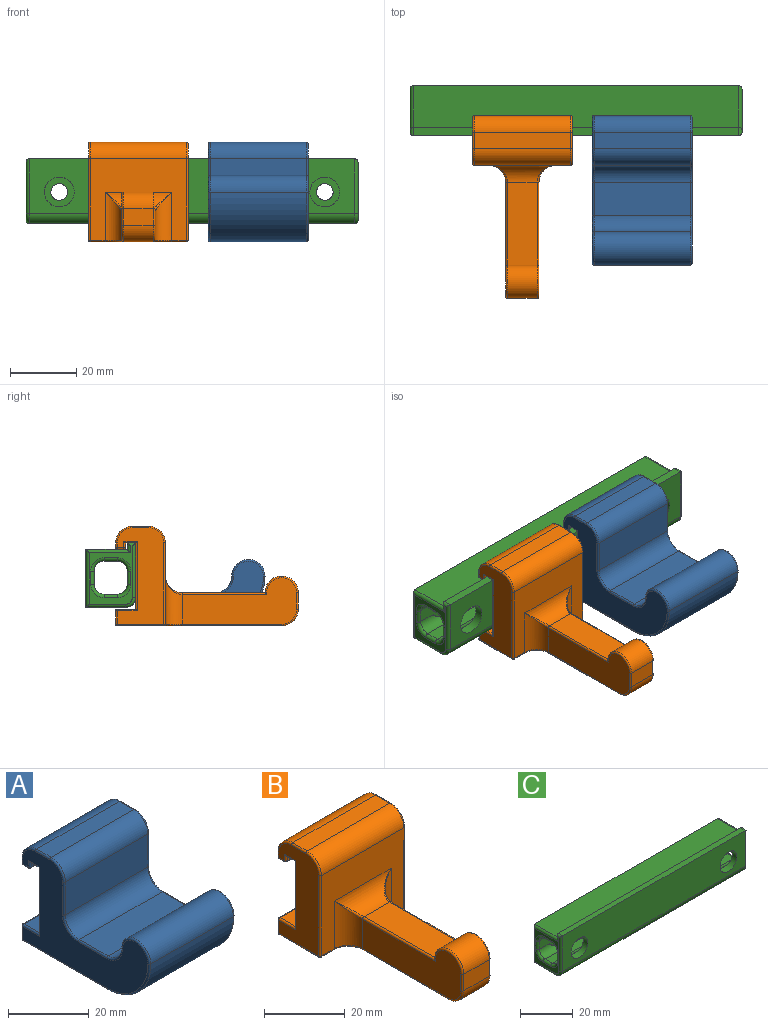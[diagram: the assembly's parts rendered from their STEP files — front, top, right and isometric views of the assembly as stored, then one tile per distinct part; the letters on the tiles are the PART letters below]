
ASSEMBLY  parts=3 mates=4
PART A: 65 faces, bbox 30x46.6x31.6 mm
  f0: plane 29x10mm, normal (0,-1,0), area 290mm2, adj f16,f18,f34,f50
  f1: plane 29x1.5mm, normal (0,1,0), area 43.5mm2, adj f17,f26,f42,f63
  f2: plane 44x29mm, normal (-1,0,0), area 594.5mm2, adj f19,f20,f21,f22,f23,f24,f25,f26
  f3: plane 29x5mm, normal (0,0,1), area 145mm2, adj f17,f18,f30,f46
  f4: plane 29.5x29mm, normal (0,0,-1), area 855.5mm2, adj f15,f25,f43,f54
  f5: plane 44x29mm, normal (1,0,0), area 594.5mm2, adj f36,f37,f38,f39,f40,f41,f42,f43
  f6: plane 29x4mm, normal (0,1,0), area 116mm2, adj f23,f41,f54,f57
  f7: plane 29x2mm, normal (0,0,-1), area 58mm2, adj f24,f40,f60,f63
  f8: plane 29x1.5mm, normal (0,-1,0), area 43.5mm2, adj f9,f22,f38,f60
  f9: plane 29x3mm, normal (0,0,-1), area 87mm2, adj f8,f10,f20,f36
  f10: plane 29x20mm, normal (0,1,0), area 580mm2, adj f9,f11,f19,f37
  f11: plane 29x5.5mm, normal (0,0,1), area 159.5mm2, adj f10,f21,f39,f57
  f12: plane 29x10mm, normal (0,0,1), area 290mm2, adj f13,f16,f33,f51
  f13: cylinder r=5mm len=29mm, axis (1,0,0), area 227.8mm2, adj f12,f14,f31,f49
  f14: cylinder r=5mm len=29mm, axis (1,0,0), area 455.5mm2, adj f13,f15,f29,f47
  f15: cylinder r=15mm len=29mm, axis (1,0,0), area 683.3mm2, adj f4,f14,f27,f45
  f16: cylinder r=5mm len=29mm, axis (-1,0,0), area 227.8mm2, adj f0,f12,f35,f52
  f17: cylinder r=5mm len=29mm, axis (-1,0,0), area 227.8mm2, adj f1,f3,f28,f44
  f18: cylinder r=5mm len=29mm, axis (1,0,0), area 227.8mm2, adj f0,f3,f32,f48
  f19: cylinder r=0.5mm len=21mm, axis (0,0,-1), area 16mm2, adj f2,f10,f20,f21
  f20: cylinder r=0.5mm len=4mm, axis (0,-1,0), area 2.6mm2, adj f2,f9,f19,f22
  f21: cylinder r=0.5mm len=6mm, axis (0,1,0), area 4.5mm2, adj f2,f11,f19,f58
  f22: cylinder r=0.5mm len=2mm, axis (0,0,1), area 1.3mm2, adj f2,f8,f20,f61
  f23: cylinder r=0.5mm len=4mm, axis (0,0,-1), area 3.1mm2, adj f2,f6,f55,f58
  f24: cylinder r=0.5mm len=2mm, axis (0,-1,0), area 1.6mm2, adj f2,f7,f61,f64
  f25: cylinder r=0.5mm len=29.5mm, axis (0,-1,0), area 23.2mm2, adj f2,f4,f27,f55
  f26: cylinder r=0.5mm len=1.5mm, axis (0,0,-1), area 1.2mm2, adj f1,f2,f28,f64
  f27: torus R=14.5mm, axis (-1,0,0), area 18.3mm2, adj f2,f15,f25,f29
  f28: torus R=4.5mm, axis (-1,0,0), area 5.9mm2, adj f2,f17,f26,f30
  f29: torus R=4.5mm, axis (-1,0,0), area 11.9mm2, adj f2,f14,f27,f31
  f30: cylinder r=0.5mm len=5mm, axis (0,1,0), area 3.9mm2, adj f2,f3,f28,f32
  f31: torus R=5.5mm, axis (-1,0,0), area 6.4mm2, adj f2,f13,f29,f33
  f32: torus R=4.5mm, axis (-1,0,0), area 5.9mm2, adj f2,f18,f30,f34
  f33: cylinder r=0.5mm len=10mm, axis (0,-1,0), area 7.9mm2, adj f2,f12,f31,f35
  f34: cylinder r=0.5mm len=10mm, axis (0,0,1), area 7.9mm2, adj f0,f2,f32,f35
  f35: torus R=5.5mm, axis (-1,0,0), area 6.4mm2, adj f2,f16,f33,f34
  f36: cylinder r=0.5mm len=4mm, axis (0,-1,0), area 2.6mm2, adj f5,f9,f37,f38
  f37: cylinder r=0.5mm len=21mm, axis (0,0,-1), area 16mm2, adj f5,f10,f36,f39
  f38: cylinder r=0.5mm len=2mm, axis (0,0,1), area 1.3mm2, adj f5,f8,f36,f59
  f39: cylinder r=0.5mm len=6mm, axis (0,1,0), area 4.5mm2, adj f5,f11,f37,f56
  f40: cylinder r=0.5mm len=2mm, axis (0,-1,0), area 1.6mm2, adj f5,f7,f59,f62
  f41: cylinder r=0.5mm len=4mm, axis (0,0,1), area 3.1mm2, adj f5,f6,f53,f56
  f42: cylinder r=0.5mm len=1.5mm, axis (0,0,1), area 1.2mm2, adj f1,f5,f44,f62
  f43: cylinder r=0.5mm len=29.5mm, axis (0,1,0), area 23.2mm2, adj f4,f5,f45,f53
  f44: torus R=4.5mm, axis (-1,0,0), area 5.9mm2, adj f5,f17,f42,f46
  f45: torus R=14.5mm, axis (-1,0,0), area 18.3mm2, adj f5,f15,f43,f47
  f46: cylinder r=0.5mm len=5mm, axis (0,-1,0), area 3.9mm2, adj f3,f5,f44,f48
  f47: torus R=4.5mm, axis (-1,0,0), area 11.9mm2, adj f5,f14,f45,f49
  f48: torus R=4.5mm, axis (-1,0,0), area 5.9mm2, adj f5,f18,f46,f50
  f49: torus R=5.5mm, axis (-1,0,0), area 6.4mm2, adj f5,f13,f47,f51
  f50: cylinder r=0.5mm len=10mm, axis (0,0,-1), area 7.9mm2, adj f0,f5,f48,f52
  f51: cylinder r=0.5mm len=10mm, axis (0,1,0), area 7.9mm2, adj f5,f12,f49,f52
  f52: torus R=5.5mm, axis (-1,0,0), area 6.4mm2, adj f5,f16,f50,f51
  f53: sphere r=0.5mm, area 0.4mm2, adj f41,f43,f54
  f54: cylinder r=0.5mm len=29mm, axis (1,0,0), area 22.8mm2, adj f4,f6,f53,f55
  f55: sphere r=0.5mm, area 0.4mm2, adj f23,f25,f54
  f56: sphere r=0.5mm, area 0.4mm2, adj f39,f41,f57
  f57: cylinder r=0.5mm len=29mm, axis (-1,0,0), area 22.8mm2, adj f6,f11,f56,f58
  f58: sphere r=0.5mm, area 0.4mm2, adj f21,f23,f57
  f59: sphere r=0.5mm, area 0.4mm2, adj f38,f40,f60
  f60: cylinder r=0.5mm len=29mm, axis (1,0,0), area 22.8mm2, adj f7,f8,f59,f61
  f61: sphere r=0.5mm, area 0.4mm2, adj f22,f24,f60
  f62: sphere r=0.5mm, area 0.4mm2, adj f40,f42,f63
  f63: cylinder r=0.5mm len=29mm, axis (-1,0,0), area 22.8mm2, adj f1,f7,f62,f64
  f64: sphere r=0.5mm, area 0.4mm2, adj f24,f26,f63
PART B: 77 faces, bbox 30x55.8x30.8 mm
  f0: plane 25x9mm, normal (0,0,1), area 225mm2, adj f16,f19,f24,f59
  f1: plane 29x24.5mm, normal (0,-1,0), area 420.5mm2, adj f17,f18,f19,f22,f43,f44,f72,f76
  f2: plane 29x1.5mm, normal (0,1,0), area 43.5mm2, adj f21,f36,f48,f58
  f3: plane 29x14mm, normal (-1,0,0), area 275.3mm2, adj f40,f46,f47,f51,f57,f58,f62,f65
  f4: plane 29x5mm, normal (0,0,1), area 145mm2, adj f21,f22,f32,f66
  f5: plane 49.5x29mm, normal (0,0,-1), area 738.5mm2, adj f20,f31,f37,f43,f54,f64,f71,f73
  f6: plane 29x14mm, normal (1,0,0), area 275.3mm2, adj f27,f30,f32,f33,f35,f36,f38,f39
  f7: plane 29x4mm, normal (0,1,0), area 116mm2, adj f55,f56,f64,f65
  f8: plane 29x2mm, normal (0,0,-1), area 58mm2, adj f34,f35,f47,f48
  f9: plane 29x1.5mm, normal (0,-1,0), area 43.5mm2, adj f10,f27,f34,f40
  f10: plane 29x3mm, normal (0,0,-1), area 87mm2, adj f9,f11,f33,f46
  f11: plane 29x20mm, normal (0,1,0), area 580mm2, adj f10,f12,f39,f51
  f12: plane 29x5.5mm, normal (0,0,1), area 159.5mm2, adj f11,f45,f56,f57
  f13: plane 34.5x14mm, normal (1,0,0), area 342.5mm2, adj f18,f24,f25,f26,f29,f31
  f14: plane 34.5x14mm, normal (-1,0,0), area 342.5mm2, adj f17,f59,f63,f67,f70,f73
  f15: plane 9x5mm, normal (0,-1,0), area 45mm2, adj f16,f20,f26,f67
  f16: cylinder r=5mm len=10mm, axis (-1,0,0), area 141.4mm2, adj f0,f15,f25,f63
  f17: cylinder r=5mm len=14.5mm, axis (0,0,-1), area 86.4mm2, adj f1,f14,f53,f75
  f18: cylinder r=5mm len=14.5mm, axis (0,0,1), area 86.4mm2, adj f1,f13,f23,f37
  f19: cylinder r=5mm len=20mm, axis (-1,0,0), area 102.1mm2, adj f0,f1,f23,f53
  f20: cylinder r=5mm len=9mm, axis (-1,0,0), area 70.7mm2, adj f5,f15,f29,f70
  f21: cylinder r=5mm len=29mm, axis (-1,0,0), area 227.8mm2, adj f2,f4,f30,f62
  f22: cylinder r=5mm len=29mm, axis (1,0,0), area 227.8mm2, adj f1,f4,f38,f69
  f23: bspline ~5.65x5.5mm, area 4.4mm2, adj f18,f19,f24
  f24: cylinder r=0.5mm len=25.53mm, axis (0,-1,0), area 19.8mm2, adj f0,f13,f23,f25
  f25: torus R=4.5mm, axis (-1,0,0), area 12mm2, adj f13,f16,f24,f26
  f26: cylinder r=0.5mm len=5mm, axis (0,0,-1), area 3.9mm2, adj f13,f15,f25,f29
  f27: cylinder r=0.5mm len=2mm, axis (0,0,1), area 1.3mm2, adj f6,f9,f28,f33
  f28: sphere r=0.5mm, area 0.4mm2, adj f27,f34,f35
  f29: torus R=4.5mm, axis (-1,0,0), area 5.9mm2, adj f13,f20,f26,f31
  f30: torus R=4.5mm, axis (-1,0,0), area 5.9mm2, adj f6,f21,f32,f36
  f31: cylinder r=0.5mm len=30mm, axis (0,1,0), area 23.6mm2, adj f5,f13,f29,f37
  f32: cylinder r=0.5mm len=5mm, axis (0,-1,0), area 3.9mm2, adj f4,f6,f30,f38
  f33: cylinder r=0.5mm len=4mm, axis (0,-1,0), area 2.6mm2, adj f6,f10,f27,f39
  f34: cylinder r=0.5mm len=29mm, axis (1,0,0), area 22.8mm2, adj f8,f9,f28,f41
  f35: cylinder r=0.5mm len=2mm, axis (0,-1,0), area 1.6mm2, adj f6,f8,f28,f42
  f36: cylinder r=0.5mm len=1.5mm, axis (0,0,1), area 1.2mm2, adj f2,f6,f30,f42
  f37: torus R=5.5mm, axis (0,0,1), area 6.4mm2, adj f5,f18,f31,f43
  f38: torus R=4.5mm, axis (-1,0,0), area 5.9mm2, adj f6,f22,f32,f44
  f39: cylinder r=0.5mm len=21mm, axis (0,0,-1), area 16mm2, adj f6,f11,f33,f45
  f40: cylinder r=0.5mm len=2mm, axis (0,0,1), area 1.3mm2, adj f3,f9,f41,f46
  f41: sphere r=0.5mm, area 0.4mm2, adj f34,f40,f47
  f42: sphere r=0.5mm, area 0.4mm2, adj f35,f36,f48
  f43: cylinder r=0.5mm len=4.5mm, axis (-1,0,0), area 3.5mm2, adj f1,f5,f37,f49
  f44: cylinder r=0.5mm len=24.5mm, axis (0,0,-1), area 19.2mm2, adj f1,f6,f38,f49
  f45: cylinder r=0.5mm len=6mm, axis (0,1,0), area 4.5mm2, adj f6,f12,f39,f50
  f46: cylinder r=0.5mm len=4mm, axis (0,-1,0), area 2.6mm2, adj f3,f10,f40,f51
  f47: cylinder r=0.5mm len=2mm, axis (0,-1,0), area 1.6mm2, adj f3,f8,f41,f52
  f48: cylinder r=0.5mm len=29mm, axis (-1,0,0), area 22.8mm2, adj f2,f8,f42,f52
  f49: sphere r=0.5mm, area 0.4mm2, adj f43,f44,f54
  f50: sphere r=0.5mm, area 0.4mm2, adj f45,f55,f56
  f51: cylinder r=0.5mm len=21mm, axis (0,0,-1), area 16mm2, adj f3,f11,f46,f57
  f52: sphere r=0.5mm, area 0.4mm2, adj f47,f48,f58
  f53: bspline ~5.65x5.5mm, area 4.4mm2, adj f17,f19,f59
  f54: cylinder r=0.5mm len=14mm, axis (0,1,0), area 11mm2, adj f5,f6,f49,f60
  f55: cylinder r=0.5mm len=4mm, axis (0,0,1), area 3.1mm2, adj f6,f7,f50,f60
  f56: cylinder r=0.5mm len=29mm, axis (-1,0,0), area 22.8mm2, adj f7,f12,f50,f61
  f57: cylinder r=0.5mm len=6mm, axis (0,1,0), area 4.5mm2, adj f3,f12,f51,f61
  f58: cylinder r=0.5mm len=1.5mm, axis (0,0,-1), area 1.2mm2, adj f2,f3,f52,f62
  f59: cylinder r=0.5mm len=25.53mm, axis (0,1,0), area 19.8mm2, adj f0,f14,f53,f63
  f60: sphere r=0.5mm, area 0.4mm2, adj f54,f55,f64
  f61: sphere r=0.5mm, area 0.4mm2, adj f56,f57,f65
  f62: torus R=4.5mm, axis (-1,0,0), area 5.9mm2, adj f3,f21,f58,f66
  f63: torus R=4.5mm, axis (-1,0,0), area 12mm2, adj f14,f16,f59,f67
  f64: cylinder r=0.5mm len=29mm, axis (1,0,0), area 22.8mm2, adj f5,f7,f60,f68
  f65: cylinder r=0.5mm len=4mm, axis (0,0,-1), area 3.1mm2, adj f3,f7,f61,f68
  f66: cylinder r=0.5mm len=5mm, axis (0,1,0), area 3.9mm2, adj f3,f4,f62,f69
  f67: cylinder r=0.5mm len=5mm, axis (0,0,1), area 3.9mm2, adj f14,f15,f63,f70
  f68: sphere r=0.5mm, area 0.4mm2, adj f64,f65,f71
  f69: torus R=4.5mm, axis (-1,0,0), area 5.9mm2, adj f3,f22,f66,f72
  f70: torus R=4.5mm, axis (-1,0,0), area 5.9mm2, adj f14,f20,f67,f73
  f71: cylinder r=0.5mm len=14mm, axis (0,-1,0), area 11mm2, adj f3,f5,f68,f74
  f72: cylinder r=0.5mm len=24.5mm, axis (0,0,1), area 19.2mm2, adj f1,f3,f69,f74
  f73: cylinder r=0.5mm len=30mm, axis (0,-1,0), area 23.6mm2, adj f5,f14,f70,f75
  f74: sphere r=0.5mm, area 0.4mm2, adj f71,f72,f76
  f75: torus R=5.5mm, axis (0,0,1), area 6.4mm2, adj f5,f17,f73,f76
  f76: cylinder r=0.5mm len=4.5mm, axis (-1,0,0), area 3.5mm2, adj f1,f5,f74,f75
PART C: 61 faces, bbox 100x15.2x19.7 mm
  f0: plane 5.26x4mm, normal (0,1,0), area 18.7mm2, adj f13,f14,f46,f59
  f1: plane 72.52x4mm, normal (0,1,0), area 285.5mm2, adj f4,f13,f59,f60
  f2: plane 5.26x4mm, normal (0,1,0), area 18.7mm2, adj f3,f13,f38,f60
  f3: cylinder r=3mm len=9mm, axis (-1,0,0), area 30.7mm2, adj f2,f15,f37,f60
  f4: cylinder r=3mm len=80mm, axis (-1,0,0), area 353.6mm2, adj f1,f15,f59,f60
  f5: cylinder r=3mm len=80mm, axis (-1,0,0), area 353.6mm2, adj f15,f17,f55,f56
  f6: cylinder r=3mm len=9mm, axis (-1,0,0), area 30.7mm2, adj f15,f17,f49,f55
  f7: plane 98x17.5mm, normal (0,1,0), area 1675.7mm2, adj f8,f19,f26,f32,f53,f54
  f8: plane 98x12.5mm, normal (0,0,1), area 1225mm2, adj f7,f9,f24,f30
  f9: plane 98x2mm, normal (0,1,0), area 196mm2, adj f8,f10,f23,f31
  f10: plane 98x2.5mm, normal (0,0,1), area 245mm2, adj f9,f11,f25,f33
  f11: plane 98x16.5mm, normal (0,-1,0), area 1489.8mm2, adj f10,f22,f27,f35,f59,f60
  f12: plane 98x4mm, normal (0,0,1), area 392mm2, adj f13,f18,f42,f50
  f13: cylinder r=3mm len=98mm, axis (-1,0,0), area 439.4mm2, adj f0,f1,f2,f12,f40,f48,f59,f60
  f14: cylinder r=3mm len=9mm, axis (-1,0,0), area 30.7mm2, adj f0,f15,f45,f59
  f15: plane 98x4mm, normal (0,0,-1), area 392mm2, adj f3,f4,f5,f6,f14,f16,f39,f47
  f16: cylinder r=3mm len=9mm, axis (-1,0,0), area 30.7mm2, adj f15,f17,f41,f56
  f17: plane 98x9mm, normal (0,-1,0), area 410.9mm2, adj f5,f6,f16,f18,f43,f51,f53,f54
  f18: cylinder r=3mm len=98mm, axis (-1,0,0), area 439.4mm2, adj f12,f17,f44,f52,f57,f58
  f19: plane 98x12mm, normal (0,0,-1), area 1176mm2, adj f7,f22,f28,f34
  f20: plane 17.5x13mm, normal (1,0,0), area 71.4mm2, adj f23,f24,f25,f26,f27,f28,f29,f45
  f21: plane 17.5x13mm, normal (-1,0,0), area 71.4mm2, adj f30,f31,f32,f33,f34,f35,f36,f37
  f22: cylinder r=3mm len=98mm, axis (-1,0,0), area 461.8mm2, adj f11,f19,f29,f36
  f23: cylinder r=1mm len=3mm, axis (0,0,-1), area 3.1mm2, adj f9,f20,f24,f25
  f24: cylinder r=1mm len=13.5mm, axis (0,1,0), area 19.6mm2, adj f8,f20,f23,f26
  f25: cylinder r=1mm len=2.5mm, axis (0,1,0), area 2.8mm2, adj f10,f20,f23,f27
  f26: cylinder r=1mm len=17.5mm, axis (0,0,-1), area 26.3mm2, adj f7,f20,f24,f28
  f27: cylinder r=1mm len=16.5mm, axis (0,0,1), area 25.3mm2, adj f11,f20,f25,f29
  f28: cylinder r=1mm len=12mm, axis (0,-1,0), area 18.3mm2, adj f19,f20,f26,f29
  f29: torus R=2mm, axis (1,0,0), area 6.5mm2, adj f20,f22,f27,f28
  f30: cylinder r=1mm len=13.5mm, axis (0,-1,0), area 19.6mm2, adj f8,f21,f31,f32
  f31: cylinder r=1mm len=3mm, axis (0,0,1), area 3.1mm2, adj f9,f21,f30,f33
  f32: cylinder r=1mm len=17.5mm, axis (0,0,1), area 26.3mm2, adj f7,f21,f30,f34
  f33: cylinder r=1mm len=2.5mm, axis (0,-1,0), area 2.8mm2, adj f10,f21,f31,f35
  f34: cylinder r=1mm len=12mm, axis (0,1,0), area 18.3mm2, adj f19,f21,f32,f36
  f35: cylinder r=1mm len=16.5mm, axis (0,0,-1), area 25.3mm2, adj f11,f21,f33,f36
  f36: torus R=2mm, axis (1,0,0), area 6.5mm2, adj f21,f22,f34,f35
  f37: torus R=4mm, axis (1,0,0), area 8.3mm2, adj f3,f21,f38,f39
  f38: cylinder r=1mm len=4mm, axis (0,0,1), area 6.3mm2, adj f2,f21,f37,f40
  f39: cylinder r=1mm len=4mm, axis (0,1,0), area 6.3mm2, adj f15,f21,f37,f41
  f40: torus R=4mm, axis (1,0,0), area 8.3mm2, adj f13,f21,f38,f42
  f41: torus R=4mm, axis (1,0,0), area 8.3mm2, adj f16,f21,f39,f43
  f42: cylinder r=1mm len=4mm, axis (0,-1,0), area 6.3mm2, adj f12,f21,f40,f44
  f43: cylinder r=1mm len=4mm, axis (0,0,-1), area 6.3mm2, adj f17,f21,f41,f44
  f44: torus R=4mm, axis (1,0,0), area 8.3mm2, adj f18,f21,f42,f43
  f45: torus R=4mm, axis (1,0,0), area 8.3mm2, adj f14,f20,f46,f47
  f46: cylinder r=1mm len=4mm, axis (0,0,-1), area 6.3mm2, adj f0,f20,f45,f48
  f47: cylinder r=1mm len=4mm, axis (0,-1,0), area 6.3mm2, adj f15,f20,f45,f49
  f48: torus R=4mm, axis (1,0,0), area 8.3mm2, adj f13,f20,f46,f50
  f49: torus R=4mm, axis (1,0,0), area 8.3mm2, adj f6,f20,f47,f51
  f50: cylinder r=1mm len=4mm, axis (0,1,0), area 6.3mm2, adj f12,f20,f48,f52
  f51: cylinder r=1mm len=4mm, axis (0,0,1), area 6.3mm2, adj f17,f20,f49,f52
  f52: torus R=4mm, axis (1,0,0), area 8.3mm2, adj f18,f20,f50,f51
  f53: cylinder r=2.5mm len=5mm, axis (0,1,0), area 39.3mm2, adj f7,f17
  f54: cylinder r=2.5mm len=5mm, axis (0,1,0), area 39.3mm2, adj f7,f17
  f55: cylinder r=4.5mm len=8.49mm, axis (0,-1,0), area 12.4mm2, adj f5,f6,f17
  f56: cylinder r=4.5mm len=8.49mm, axis (0,-1,0), area 12.4mm2, adj f5,f16,f17
  f57: cylinder r=4.5mm len=7.48mm, axis (0,-1,0), area 3.4mm2, adj f17,f18
  f58: cylinder r=4.5mm len=7.48mm, axis (0,-1,0), area 3.4mm2, adj f17,f18
  f59: cylinder r=4.5mm len=9mm, axis (0,-1,0), area 86.5mm2, adj f0,f1,f4,f11,f13,f14
  f60: cylinder r=4.5mm len=9mm, axis (0,-1,0), area 86.5mm2, adj f1,f2,f3,f4,f11,f13
PLACE A t=(-45.05,5,-8.5)mm
PLACE B t=(-81.15,5,-8.5)mm
PLACE C t=(-100,14,-3)mm
MATE planar B.f11 <-> C.f11  axis (0,1,0) through (-66.15,-1,6.5)mm
MATE planar A.f10 <-> C.f11  axis (0,1,0) through (-30.05,-1,6.5)mm
MATE planar A.f7 <-> C.f8  axis (0,0,-1) through (-30.05,3.5,14.5)mm
MATE planar B.f8 <-> C.f8  axis (0,0,-1) through (-66.15,3.5,14.5)mm
